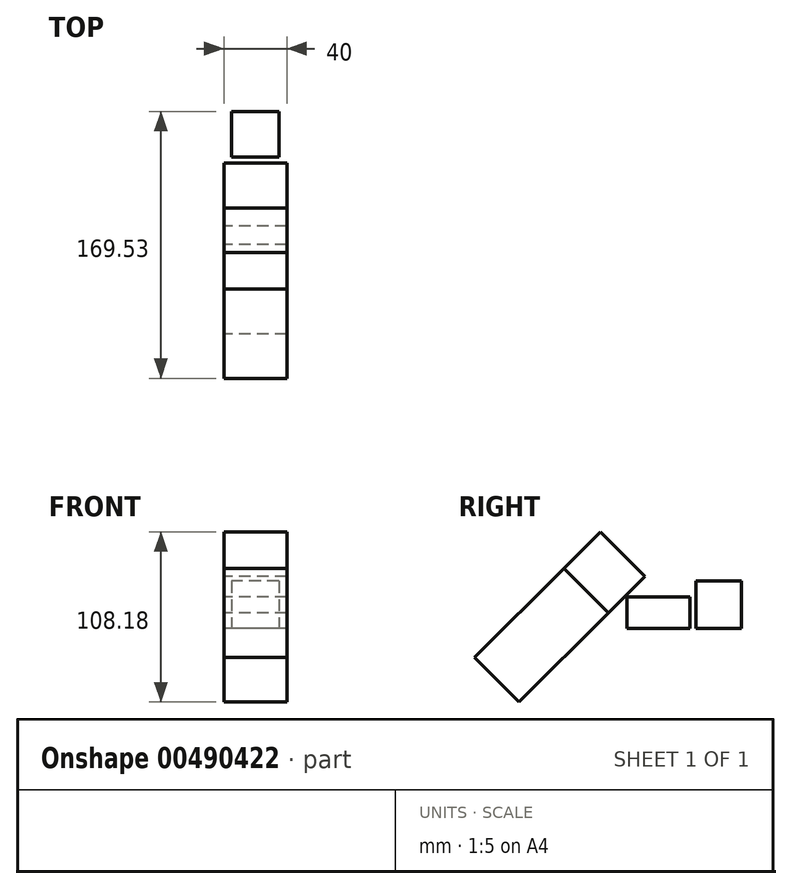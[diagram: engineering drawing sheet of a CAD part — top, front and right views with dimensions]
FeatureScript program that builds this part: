
annotation { "Feature Type Name" : "Feature", "Feature Type Description" : "" }
export const myFeature = defineFeature(function(context is Context, id is Id, definition is map)
    precondition{}
    {
        {
            var Q0;
            Q0=qCreatedBy(makeId("Top.planeOp"),FACE);
            var sketch = newSketch(context, id + "F0", { "sketchPlane" : qUnion([Q0])});
            skLineSegment(sketch, "E0.bottom", {"start": v(15.25, 15.25) * mm, "end": v(-15.25, 15.25) * mm, "construction": true});
            skLineSegment(sketch, "E0.top", {"start": v(15.25, -15.25) * mm, "end": v(-15.25, -15.25) * mm, "construction": true});
            skLineSegment(sketch, "E0.left", {"start": v(15.25, 15.25) * mm, "end": v(15.25, -15.25) * mm, "construction": true});
            skLineSegment(sketch, "E0.right", {"start": v(-15.25, 15.25) * mm, "end": v(-15.25, -15.25) * mm, "construction": true});
            skPoint(sketch, "E0.middle", {"position": v(0, 0) * mm});
            skCircle(sketch, "E1", {"center": v(15.25, 15.25) * mm, "radius": 1.57 * mm, "construction": true});
            skCircle(sketch, "E2", {"center": v(-15.25, 15.25) * mm, "radius": 1.57 * mm, "construction": true});
            skCircle(sketch, "E3", {"center": v(-15.25, -15.25) * mm, "radius": 1.57 * mm, "construction": true});
            skCircle(sketch, "E4", {"center": v(15.25, -15.25) * mm, "radius": 1.57 * mm, "construction": true});
            skLineSegment(sketch, "E5.bottom", {"start": v(18, 18) * mm, "end": v(-18, 18) * mm, "construction": true});
            skLineSegment(sketch, "E5.top", {"start": v(18, -18) * mm, "end": v(-18, -18) * mm, "construction": true});
            skLineSegment(sketch, "E5.left", {"start": v(18, 18) * mm, "end": v(18, -18) * mm, "construction": true});
            skLineSegment(sketch, "E5.right", {"start": v(-18, 18) * mm, "end": v(-18, -18) * mm, "construction": true});
            skLineSegment(sketch, "E6", {"start": v(0, 71.85) * mm, "end": v(0, -68.44) * mm, "construction": true});
            skLineSegment(sketch, "E7", {"start": v(63.09, 0) * mm, "end": v(-70.76, 0) * mm, "construction": true});
            skLineSegment(sketch, "E8", {"start": v(70.7, 84.26) * mm, "end": v(-70.7, -84.26) * mm, "construction": true});
            skLineSegment(sketch, "E9", {"start": v(-70.7, 84.26) * mm, "end": v(70.7, -84.26) * mm, "construction": true});
            skCircle(sketch, "E10", {"center": v(70.7, 84.26) * mm, "radius": 64.77 * mm, "construction": true});
            skCircle(sketch, "E11", {"center": v(-70.7, 84.26) * mm, "radius": 64.77 * mm, "construction": true});
            skCircle(sketch, "E12", {"center": v(-70.7, -84.26) * mm, "radius": 64.77 * mm, "construction": true});
            skCircle(sketch, "E13", {"center": v(70.7, -84.26) * mm, "radius": 64.77 * mm, "construction": true});
            skPoint(sketch, "E14.middle", {"position": v(0, 52.02) * mm});
            skSolve(sketch);
        }
        {
            var Q0;
            Q0=qCreatedBy(makeId("Right.planeOp"),FACE);
            var sketch = newSketch(context, id + "F1", { "sketchPlane" : qUnion([Q0])});
            skLineSegment(sketch, "E15", {"start": v(0, 0) * mm, "end": v(-2.84, 0) * mm, "construction": true});
            skLineSegment(sketch, "E16", {"start": v(-2.84, 0) * mm, "end": v(25.6, 28.44) * mm, "construction": true});
            skSolve(sketch);
        }
        {
            var Q0;
            Q0=sQuery(id+"F1.wireOp",EDGE,"E16");
            cPlane(context, id + "F2", {"entities" : qUnion([Q0]), "cplaneType" : CPlaneType.LINE_ANGLE, "offset" : 25 * mm, "angle" : 0 * degree, "width" : 150 * mm, "height" : 150 * mm});
        }
        {
            var Q0;
            Q0=qCreatedBy(id+"F2.planeOp",FACE);
            var sketch = newSketch(context, id + "F3", { "sketchPlane" : qUnion([Q0])});
            skPoint(sketch, "E17.0", {"position": v(0, -2) * mm});
            skLineSegment(sketch, "E18", {"start": v(0, -8.27) * mm, "end": v(0, -2) * mm, "construction": true});
            skLineSegment(sketch, "E19.bottom", {"start": v(20, 31.73) * mm, "end": v(-20, 31.73) * mm});
            skLineSegment(sketch, "E19.top", {"start": v(20, -48.27) * mm, "end": v(-20, -48.27) * mm});
            skLineSegment(sketch, "E19.left", {"start": v(20, 31.73) * mm, "end": v(20, -48.27) * mm});
            skLineSegment(sketch, "E19.right", {"start": v(-20, 31.73) * mm, "end": v(-20, -48.27) * mm});
            skPoint(sketch, "E19.middle", {"position": v(0, -8.27) * mm});
            skSolve(sketch);
        }
        {
            var Q0;
            Q0 = qSketchRegion(id + "F3", true);
            extrude(context, id + "F4", {"entities" : qUnion([Q0]), "endBound" : BoundingType.SYMMETRIC, "depth" : 40 * mm});
        }
        {
            var Q0;
            Q0=qCreatedBy(makeId("Top.planeOp"),FACE);
            var sketch = newSketch(context, id + "F5", { "sketchPlane" : qUnion([Q0])});
            skLineSegment(sketch, "E20", {"start": v(-51.48, 0) * mm, "end": v(50.5, 0) * mm, "construction": true});
            skLineSegment(sketch, "E21", {"start": v(0, 67.1) * mm, "end": v(0, 0) * mm, "construction": true});
            skLineSegment(sketch, "E22.bottom", {"start": v(20, 87.1) * mm, "end": v(-20, 87.1) * mm});
            skLineSegment(sketch, "E22.top", {"start": v(20, 47.1) * mm, "end": v(-20, 47.1) * mm});
            skLineSegment(sketch, "E22.left", {"start": v(20, 87.1) * mm, "end": v(20, 47.1) * mm});
            skLineSegment(sketch, "E22.right", {"start": v(-20, 87.1) * mm, "end": v(-20, 47.1) * mm});
            skPoint(sketch, "E22.middle", {"position": v(0, 67.1) * mm});
            skSolve(sketch);
        }
        {
            var Q0;
            Q0=makeQuery(id+"F5.imprint","IMPRINT",FACE,{"disambiguationData":[TD([[makeQuery(id+"F5.imprint","IMPRINT",EDGE,{"derivedFrom":sQuery(id+"F5.wireOp",EDGE,"E22.bottom")}),1.0]])]});
            extrude(context, id + "F6", {"entities" : qUnion([Q0]), "depth" : 20 * mm});
        }
        {
            var Q0;
            Q0=makeQuery(id+"F4.opExtrude","SWEPT_FACE",FACE,{"disambiguationData":[OSD([sQuery(id+"F3.wireOp",EDGE,"E19.bottom")])]});
            extrude(context, id + "F7", {"entities" : qUnion([Q0]), "depth" : 33 * mm});
        }
        {
            var Q0;
            Q0=qCreatedBy(makeId("Top.planeOp"),FACE);
            var sketch = newSketch(context, id + "F8", { "sketchPlane" : qUnion([Q0])});
            skLineSegment(sketch, "E23", {"start": v(0, 0) * mm, "end": v(0, 105.33) * mm});
            skLineSegment(sketch, "E24.bottom", {"start": v(15, 119.83) * mm, "end": v(-15, 119.83) * mm});
            skLineSegment(sketch, "E24.top", {"start": v(15, 90.83) * mm, "end": v(-15, 90.83) * mm});
            skLineSegment(sketch, "E24.left", {"start": v(15, 119.83) * mm, "end": v(15, 90.83) * mm});
            skLineSegment(sketch, "E24.right", {"start": v(-15, 119.83) * mm, "end": v(-15, 90.83) * mm});
            skPoint(sketch, "E24.middle", {"position": v(0, 105.33) * mm});
            skSolve(sketch);
        }
        {
            var Q0;
            Q0=makeQuery(id+"F8.imprint","IMPRINT",FACE,{"disambiguationData":[TD([[makeQuery(id+"F8.imprint","IMPRINT",EDGE,{"derivedFrom":sQuery(id+"F8.wireOp",EDGE,"E24.bottom")}),1.0]])]});
            extrude(context, id + "F9", {"entities" : qUnion([Q0]), "depth" : 30 * mm});
        }
    });
